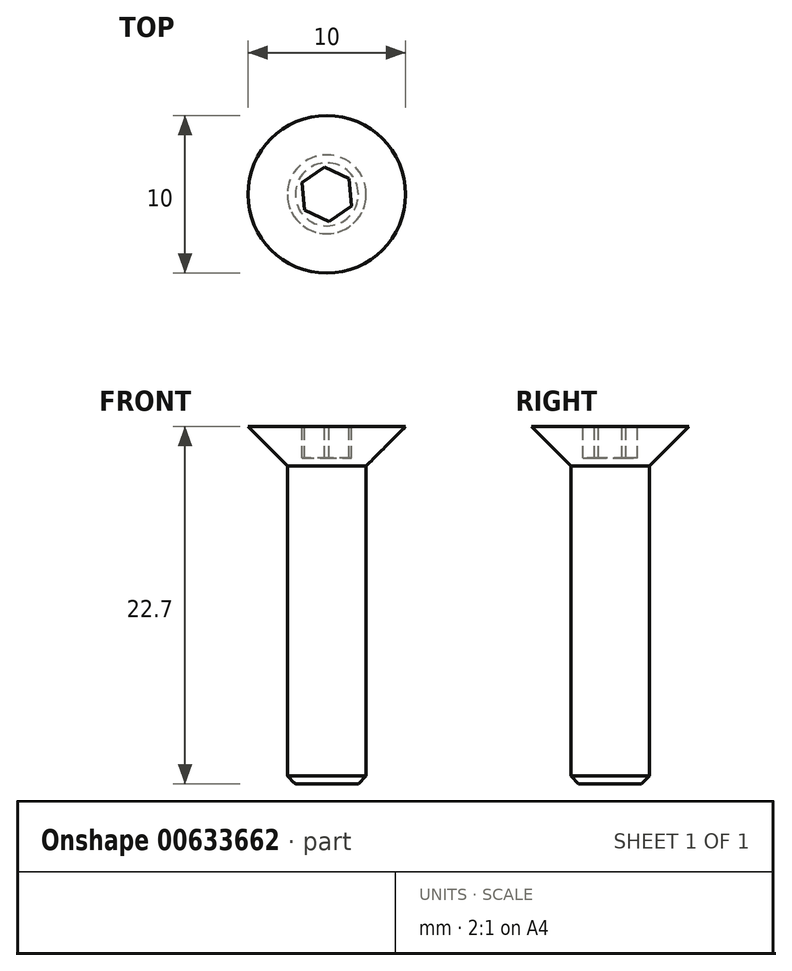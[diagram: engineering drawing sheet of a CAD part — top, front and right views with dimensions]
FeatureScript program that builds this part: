
annotation { "Feature Type Name" : "Feature", "Feature Type Description" : "" }
export const myFeature = defineFeature(function(context is Context, id is Id, definition is map)
    precondition{}
    {
        {
            var Q0;
            Q0=qCreatedBy(makeId("Top.planeOp"),FACE);
            var sketch = newSketch(context, id + "F0", { "sketchPlane" : qUnion([Q0])});
            skCircle(sketch, "E0", {"center": v(0, 0) * mm, "radius": 5 * mm});
            skSolve(sketch);
        }
        {
            var Q0;
            Q0 = qSketchRegion(id + "F0", true);
            var Q1;
            Q1=makeQuery(id+"F0.imprint","IMPRINT",FACE,{"disambiguationData":[TD([[makeQuery(id+"F0.imprint","IMPRINT",EDGE,{"derivedFrom":sQuery(id+"F0.wireOp",EDGE,"35546dd4-805c-4033-ae00-86aa25de4e10.0")}),-1.0]])]});
            extrude(context, id + "F1", {"entities" : qUnion([Q0, Q1]), "depth" : 2.7 * mm, "offsetDistance" : 25 * mm});
        }
        {
            var Q0;
            Q0=makeQuery(id+"F1.opExtrude","CAP_FACE",FACE,{"disambiguationData":[OSD([sQuery(id+"F0.wireOp",EDGE,"E0")])],"isStart":true});
            var sketch = newSketch(context, id + "F2", { "sketchPlane" : qUnion([Q0])});
            skCircle(sketch, "E1", {"center": v(0, 0) * mm, "radius": 2.5 * mm});
            skSolve(sketch);
        }
        {
            var Q0;
            Q0=makeQuery(id+"F1.opExtrude","CAP_FACE",FACE,{"disambiguationData":[OSD([sQuery(id+"F0.wireOp",EDGE,"E0")])],"isStart":false});
            var sketch = newSketch(context, id + "F3", { "sketchPlane" : qUnion([Q0])});
            skCircle(sketch, "E2.cCircle", {"center": v(0, 0) * mm, "radius": 1.5 * mm, "construction": true});
            skLineSegment(sketch, "E2.0", {"start": v(-0.15, 1.73) * mm, "end": v(1.42, 0.99) * mm});
            skLineSegment(sketch, "E2.1", {"start": v(1.42, 0.99) * mm, "end": v(1.57, -0.74) * mm});
            skLineSegment(sketch, "E2.2", {"start": v(1.57, -0.74) * mm, "end": v(0.15, -1.73) * mm});
            skLineSegment(sketch, "E2.3", {"start": v(0.15, -1.73) * mm, "end": v(-1.42, -0.99) * mm});
            skLineSegment(sketch, "E2.4", {"start": v(-1.42, -0.99) * mm, "end": v(-1.57, 0.74) * mm});
            skLineSegment(sketch, "E2.5", {"start": v(-1.57, 0.74) * mm, "end": v(-0.15, 1.73) * mm});
            skPoint(sketch, "E2.0.midPoint", {"position": v(0.64, 1.36) * mm});
            skLineSegment(sketch, "E3", {"start": v(0.64, 1.36) * mm, "end": v(0, 0) * mm, "construction": true});
            skSolve(sketch);
        }
        {
            var Q0;
            Q0=makeQuery(id+"F3.imprint","IMPRINT",FACE,{"disambiguationData":[TD([[makeQuery(id+"F3.imprint","IMPRINT",EDGE,{"derivedFrom":sQuery(id+"F3.wireOp",EDGE,"E2.0")}),-1.0]])]});
            extrude(context, id + "F4", {"entities" : qUnion([Q0]), "operationType" : NewBodyOperationType.REMOVE, "oppositeDirection" : true, "depth" : 2 * mm, "offsetDistance" : 25 * mm});
        }
        {
            var Q0;
            Q0=makeQuery(id+"F2.imprint","IMPRINT",FACE,{"disambiguationData":[TD([[makeQuery(id+"F2.imprint","IMPRINT",EDGE,{"derivedFrom":sQuery(id+"F2.wireOp",EDGE,"E1")}),1.0]])]});
            extrude(context, id + "F5", {"entities" : qUnion([Q0]), "operationType" : NewBodyOperationType.ADD, "depth" : 20 * mm, "offsetDistance" : 25 * mm});
        }
        {
            var Q0;
            Q0=makeQuery(id+"F5.opExtrude","CAP_EDGE",EDGE,{"disambiguationData":[OSD([sQuery(id+"F2.wireOp",EDGE,"E1")])],"isStart":false});
            chamfer(context, id + "F6", {"entities" : qUnion([Q0]), "width" : 0.5 * mm, "tangentPropagation" : true});
        }
        {
            var Q0;
            Q0=makeQuery(id+"F1.opExtrude","CAP_EDGE",EDGE,{"disambiguationData":[OSD([sQuery(id+"F0.wireOp",EDGE,"E0")])],"isStart":true});
            chamfer(context, id + "F7", {"entities" : qUnion([Q0]), "width" : 2.7 * mm, "tangentPropagation" : true});
        }
    });
